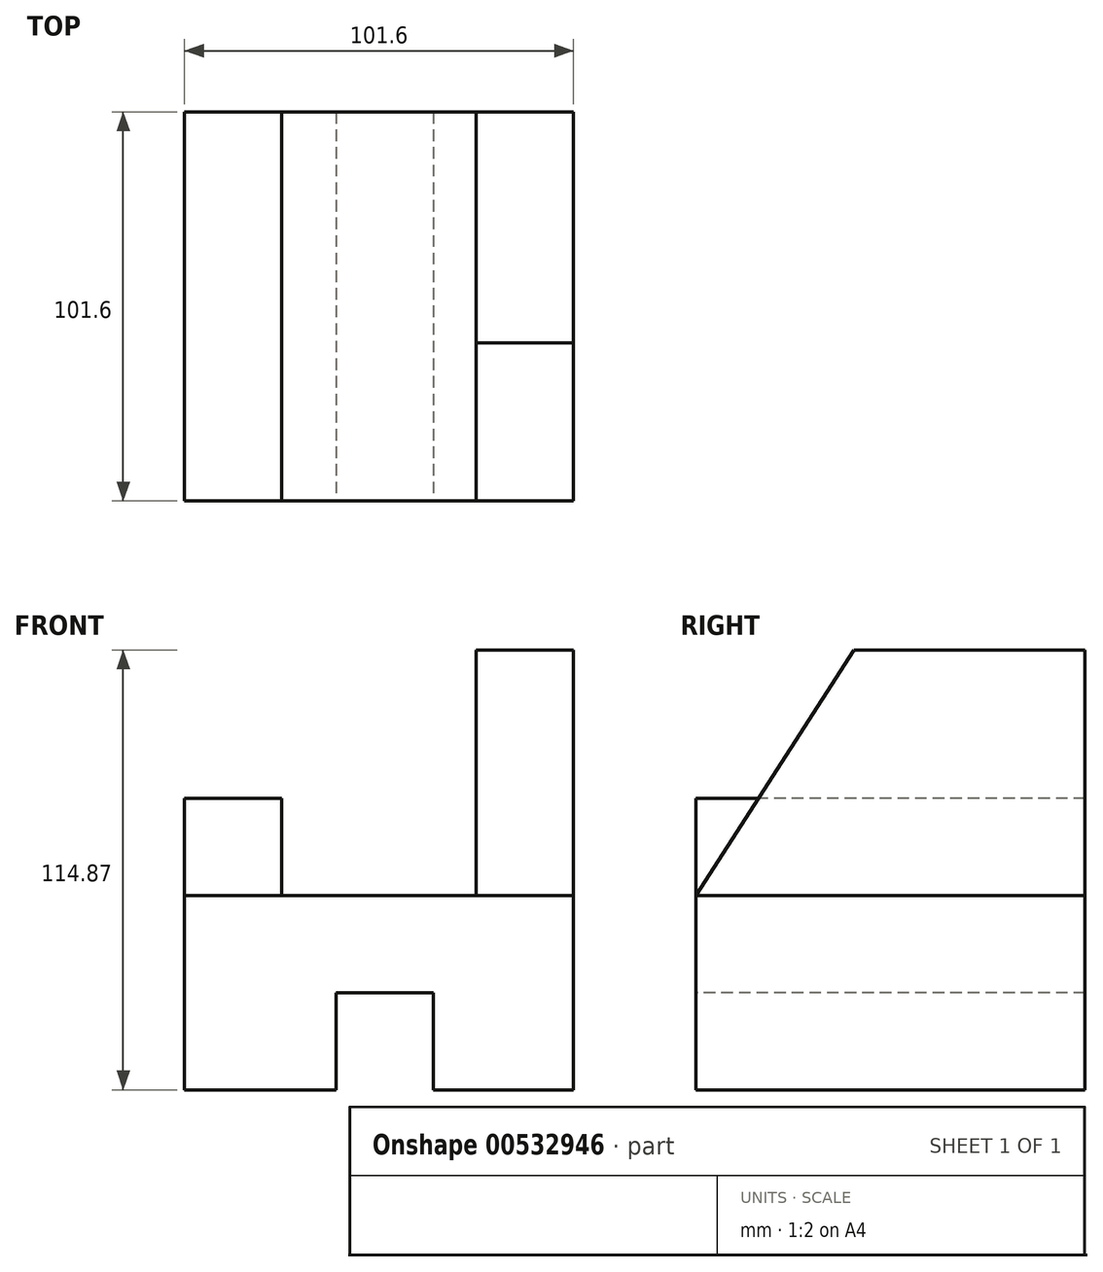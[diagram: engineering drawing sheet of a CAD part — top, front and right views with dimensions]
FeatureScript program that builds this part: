
annotation { "Feature Type Name" : "Feature", "Feature Type Description" : "" }
export const myFeature = defineFeature(function(context is Context, id is Id, definition is map)
    precondition{}
    {
        {
            var Q0;
            Q0=qCreatedBy(makeId("Right.planeOp"),FACE);
            var sketch = newSketch(context, id + "F0", { "sketchPlane" : qUnion([Q0])});
            skLineSegment(sketch, "E0", {"start": v(-65.05, 0) * mm, "end": v(36.55, 0) * mm});
            skLineSegment(sketch, "E1", {"start": v(36.55, 0) * mm, "end": v(36.55, 50.8) * mm});
            skLineSegment(sketch, "E2", {"start": v(-65.05, 0) * mm, "end": v(-65.05, 50.8) * mm});
            skLineSegment(sketch, "E3", {"start": v(-65.05, 50.8) * mm, "end": v(36.55, 50.8) * mm});
            skSolve(sketch);
        }
        {
            var Q0;
            Q0=makeQuery(id+"F0.imprint","IMPRINT",FACE,{"disambiguationData":[TD([[makeQuery(id+"F0.imprint","IMPRINT",EDGE,{"derivedFrom":sQuery(id+"F0.wireOp",EDGE,"E0")}),1.0]])]});
            extrude(context, id + "F1", {"entities" : qUnion([Q0]), "depth" : 101.6 * mm, "offsetDistance" : 25.4 * mm});
        }
        {
            var Q0;
            Q0=makeQuery(id+"F1.opExtrude","CAP_FACE",FACE,{"disambiguationData":[OSD([sQuery(id+"F0.wireOp",EDGE,"E0"),sQuery(id+"F0.wireOp",EDGE,"E1"),sQuery(id+"F0.wireOp",EDGE,"E2"),sQuery(id+"F0.wireOp",EDGE,"E3")])],"isStart":true});
            var sketch = newSketch(context, id + "F2", { "sketchPlane" : qUnion([Q0])});
            skLineSegment(sketch, "E4", {"start": v(-36.55, 50.8) * mm, "end": v(-36.55, 76.2) * mm});
            skLineSegment(sketch, "E5", {"start": v(-36.55, 76.2) * mm, "end": v(65.05, 76.2) * mm});
            skLineSegment(sketch, "E6", {"start": v(65.05, 76.2) * mm, "end": v(65.05, 50.8) * mm});
            skSolve(sketch);
        }
        {
            var Q0;
            Q0=makeQuery(id+"F2.imprint","IMPRINT",FACE,{"disambiguationData":[TD([[makeQuery(id+"F2.imprint","IMPRINT",EDGE,{"derivedFrom":sQuery(id+"F2.wireOp",EDGE,"E4")}),-1.0]])]});
            extrude(context, id + "F3", {"entities" : qUnion([Q0]), "oppositeDirection" : true, "depth" : 25.4 * mm, "offsetDistance" : 25.4 * mm});
        }
        {
            var Q0;
            Q0=makeQuery(id+"F1.opExtrude","CAP_FACE",FACE,{"disambiguationData":[OSD([sQuery(id+"F0.wireOp",EDGE,"E0"),sQuery(id+"F0.wireOp",EDGE,"E1"),sQuery(id+"F0.wireOp",EDGE,"E2"),sQuery(id+"F0.wireOp",EDGE,"E3")])],"isStart":false});
            var sketch = newSketch(context, id + "F4", { "sketchPlane" : qUnion([Q0])});
            skLineSegment(sketch, "E7", {"start": v(-65.05, 50.8) * mm, "end": v(-23.8, 114.87) * mm});
            skLineSegment(sketch, "E8", {"start": v(-23.8, 114.87) * mm, "end": v(36.55, 114.87) * mm});
            skLineSegment(sketch, "E9", {"start": v(36.55, 114.87) * mm, "end": v(36.55, 50.8) * mm});
            skSolve(sketch);
        }
        {
            var Q0;
            Q0=makeQuery(id+"F4.imprint","IMPRINT",FACE,{"disambiguationData":[TD([[makeQuery(id+"F4.imprint","IMPRINT",EDGE,{"derivedFrom":sQuery(id+"F4.wireOp",EDGE,"E7")}),-1.0]])]});
            extrude(context, id + "F5", {"entities" : qUnion([Q0]), "oppositeDirection" : true, "depth" : 25.4 * mm, "offsetDistance" : 25.4 * mm});
        }
        {
            var Q0;
            Q0=makeQuery(id+"F1.opExtrude","SWEPT_FACE",FACE,{"disambiguationData":[OSD([sQuery(id+"F0.wireOp",EDGE,"E2")])]});
            var sketch = newSketch(context, id + "F6", { "sketchPlane" : qUnion([Q0])});
            skLineSegment(sketch, "E10", {"start": v(50.8, 0) * mm, "end": v(64.98, 0) * mm});
            skLineSegment(sketch, "E11", {"start": v(64.98, 0) * mm, "end": v(64.98, 25.4) * mm});
            skLineSegment(sketch, "E12", {"start": v(64.98, 25.4) * mm, "end": v(39.58, 25.4) * mm});
            skLineSegment(sketch, "E13", {"start": v(39.58, 25.4) * mm, "end": v(39.58, 0) * mm});
            skLineSegment(sketch, "E14", {"start": v(39.58, 0) * mm, "end": v(50.8, 0) * mm});
            skSolve(sketch);
        }
        {
            var Q0;
            Q0=makeQuery(id+"F6.imprint","IMPRINT",FACE,{"disambiguationData":[TD([[makeQuery(id+"F6.imprint","IMPRINT",EDGE,{"derivedFrom":sQuery(id+"F6.wireOp",EDGE,"E10")}),-1.0]])]});
            extrude(context, id + "F7", {"entities" : qUnion([Q0]), "operationType" : NewBodyOperationType.REMOVE, "oppositeDirection" : true, "depth" : 101.6 * mm, "offsetDistance" : 25.4 * mm});
        }
    });
